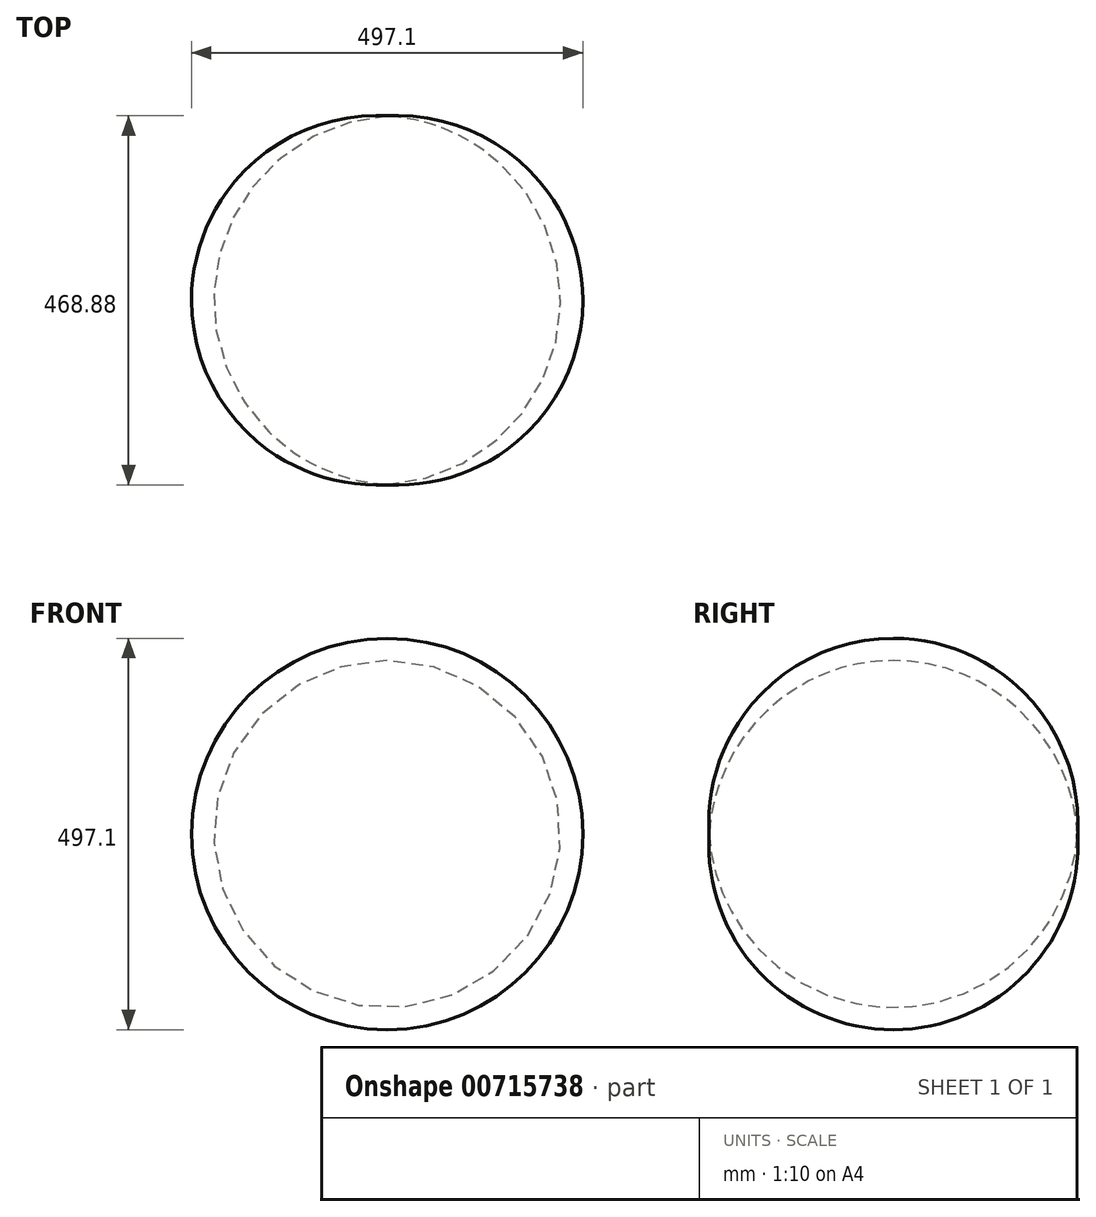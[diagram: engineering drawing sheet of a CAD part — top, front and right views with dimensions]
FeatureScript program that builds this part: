
annotation { "Feature Type Name" : "Feature", "Feature Type Description" : "" }
export const myFeature = defineFeature(function(context is Context, id is Id, definition is map)
    precondition{}
    {
        {
            var Q0;
            Q0=qCreatedBy(makeId("Top.planeOp"),FACE);
            var sketch = newSketch(context, id + "F0", { "sketchPlane" : qUnion([Q0])});
            skArc(sketch, "E0", {"start": v(0, 236) * mm, "mid": v(-220.33, 2) * mm, "end": v(0, -232.03) * mm});
            skLineSegment(sketch, "E1", {"start": v(0, -232.03) * mm, "end": v(0, 236) * mm});
            skSolve(sketch);
        }
        {
            var Q0;
            Q0 = qSketchRegion(id + "F0", true);
            var Q1;
            Q1=sQuery(id+"F0.wireOp",EDGE,"E1");
            revolve(context, id + "F1", {"surfaceOperationType" : NewSurfaceOperationType.NEW, "entities" : qUnion([Q0]), "axis" : qUnion([Q1]), "revolveType" : RevolveType.FULL});
        }
    });
